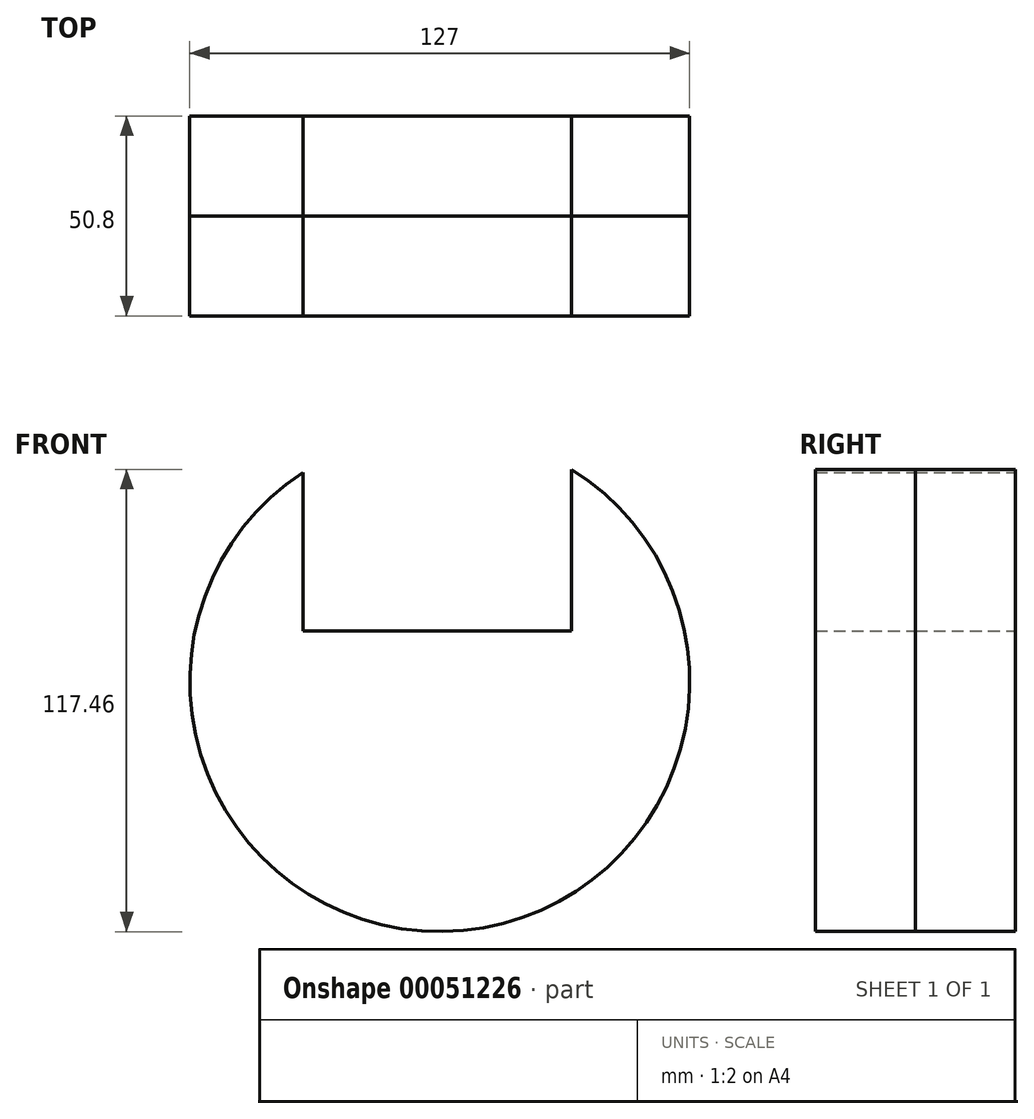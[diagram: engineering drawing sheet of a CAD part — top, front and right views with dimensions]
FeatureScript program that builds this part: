
annotation { "Feature Type Name" : "Feature", "Feature Type Description" : "" }
export const myFeature = defineFeature(function(context is Context, id is Id, definition is map)
    precondition{}
    {
        {
            var Q0;
            Q0=qCreatedBy(makeId("Front.planeOp"),FACE);
            var sketch = newSketch(context, id + "F0", { "sketchPlane" : qUnion([Q0])});
            skCircle(sketch, "E0", {"center": v(-41.55, 45.18) * mm, "radius": 63.5 * mm});
            skSolve(sketch);
        }
        {
            var Q0;
            Q0 = qSketchRegion(id + "F0", true);
            extrude(context, id + "F1", {"entities" : qUnion([Q0]), "depth" : 25.4 * mm});
        }
        {
            var Q0;
            Q0=makeQuery(id+"F1.opExtrude","CAP_FACE",FACE,{"disambiguationData":[OSD([sQuery(id+"F0.wireOp",EDGE,"E0")])],"isStart":false});
            extrude(context, id + "F2", {"entities" : qUnion([Q0]), "depth" : 25.4 * mm});
        }
        {
            var Q0;
            Q0=makeQuery(id+"F1.opExtrude","CAP_FACE",FACE,{"disambiguationData":[OSD([sQuery(id+"F0.wireOp",EDGE,"E0")])],"isStart":true});
            var sketch = newSketch(context, id + "F3", { "sketchPlane" : qUnion([Q0])});
            skLineSegment(sketch, "E1.bottom", {"start": v(8.08, 122.34) * mm, "end": v(76.27, 122.34) * mm});
            skLineSegment(sketch, "E1.top", {"start": v(8.08, 58.08) * mm, "end": v(76.27, 58.08) * mm});
            skLineSegment(sketch, "E1.left", {"start": v(8.08, 122.34) * mm, "end": v(8.08, 58.08) * mm});
            skLineSegment(sketch, "E1.right", {"start": v(76.27, 122.34) * mm, "end": v(76.27, 58.08) * mm});
            skSolve(sketch);
        }
        {
            var Q0;
            {var subQ0=sQuery(id+"F3.wireOp",EDGE,"E1.top");Q0=makeQuery(id+"F3.imprint","IMPRINT",FACE,{"disambiguationData":[TD([[makeQuery(id+"F3.imprint","IMPRINT",EDGE,{"derivedFrom":subQ0}),1.0]])]});}
            extrude(context, id + "F4", {"entities" : qUnion([Q0]), "operationType" : NewBodyOperationType.REMOVE, "oppositeDirection" : true, "depth" : 50.8 * mm});
        }
        {
            var Q0;
            Q0=makeQuery(id+"F2.opExtrude","CAP_FACE",FACE,{"disambiguationData":[OSD([sQuery(id+"F0.wireOp",EDGE,"E0")])],"isStart":true});
            var sketch = newSketch(context, id + "F5", { "sketchPlane" : qUnion([Q0])});
            skLineSegment(sketch, "E2.bottom", {"start": v(8.08, 68.08) * mm, "end": v(76.27, 68.08) * mm});
            skLineSegment(sketch, "E2.top", {"start": v(8.08, 118.08) * mm, "end": v(76.27, 118.08) * mm});
            skLineSegment(sketch, "E2.left", {"start": v(8.08, 68.08) * mm, "end": v(8.08, 118.08) * mm});
            skLineSegment(sketch, "E2.right", {"start": v(76.27, 68.08) * mm, "end": v(76.27, 118.08) * mm});
            skSolve(sketch);
        }
        {
            var Q0;
            Q0 = qSketchRegion(id + "F5", true);
            extrude(context, id + "F6", {"entities" : qUnion([Q0]), "operationType" : NewBodyOperationType.REMOVE, "oppositeDirection" : true, "depth" : 64.07 * mm});
        }
    });
